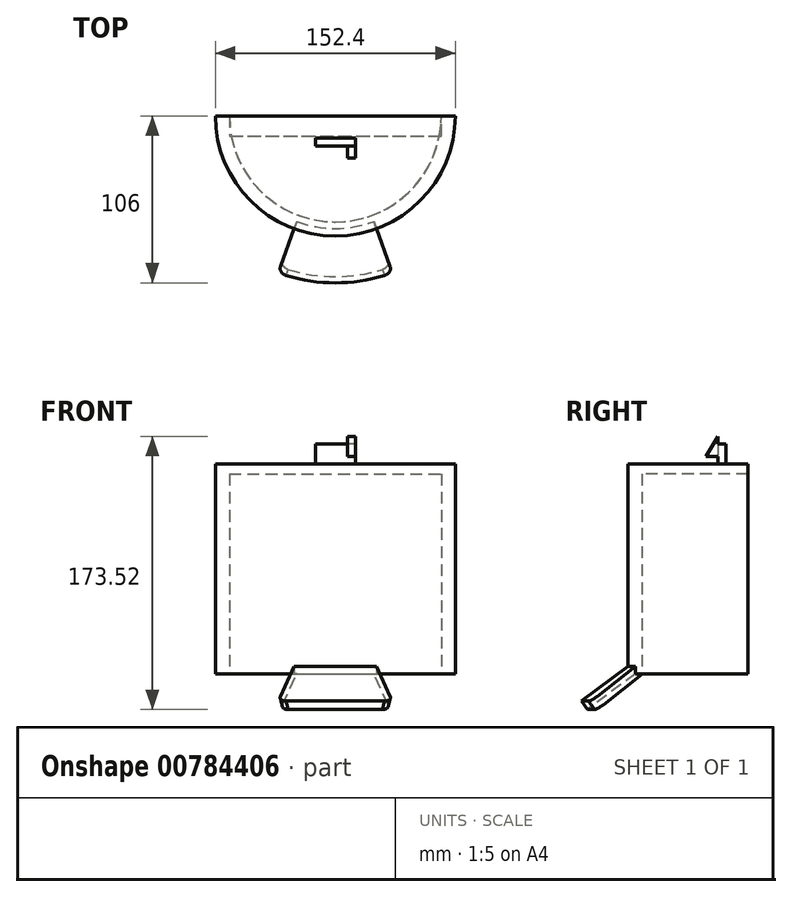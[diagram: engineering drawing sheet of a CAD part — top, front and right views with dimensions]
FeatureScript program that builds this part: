
annotation { "Feature Type Name" : "Feature", "Feature Type Description" : "" }
export const myFeature = defineFeature(function(context is Context, id is Id, definition is map)
    precondition{}
    {
        {
            var Q0;
            Q0=qCreatedBy(makeId("Top.planeOp"),FACE);
            var sketch = newSketch(context, id + "F0", { "sketchPlane" : qUnion([Q0])});
            skArc(sketch, "E0", {"start": v(76.2, 0) * mm, "mid": v(0, -76.2) * mm, "end": v(-76.2, 0) * mm});
            skLineSegment(sketch, "E1", {"start": v(-67.31, 0) * mm, "end": v(-67.31, -12.7) * mm});
            skLineSegment(sketch, "E2", {"start": v(-67.31, -12.7) * mm, "end": v(67.31, -12.7) * mm});
            skLineSegment(sketch, "E3", {"start": v(67.31, -12.7) * mm, "end": v(67.31, 0) * mm});
            skLineSegment(sketch, "E4", {"start": v(67.31, 0) * mm, "end": v(76.2, 0) * mm});
            skLineSegment(sketch, "E5", {"start": v(-76.2, 0) * mm, "end": v(-67.31, 0) * mm});
            skSolve(sketch);
        }
        {
            var Q0;
            Q0=qSketchRegion(id+"F0",true);
            extrude(context, id + "F1", {"entities" : qUnion([Q0]), "depth" : 3 / 406.4 * mm, "offsetDistance" : 25.4 * mm});
        }
        {
            var Q0;
            Q0=makeQuery(id+"F1.opExtrude","CAP_FACE",FACE,{"disambiguationData":[OSD([sQuery(id+"F0.wireOp",EDGE,"E0"),sQuery(id+"F0.wireOp",EDGE,"E1"),sQuery(id+"F0.wireOp",EDGE,"E2"),sQuery(id+"F0.wireOp",EDGE,"E3"),sQuery(id+"F0.wireOp",EDGE,"E4"),sQuery(id+"F0.wireOp",EDGE,"E5")])],"isStart":false});
            var sketch = newSketch(context, id + "F2", { "sketchPlane" : qUnion([Q0])});
            skArc(sketch, "E6", {"start": v(-76.2, 0) * mm, "mid": v(0, -76.2) * mm, "end": v(76.2, 0) * mm});
            skArc(sketch, "E7", {"start": v(-67.31, 0) * mm, "mid": v(0, -67.31) * mm, "end": v(67.31, 0) * mm});
            skLineSegment(sketch, "E8", {"start": v(-67.31, 0) * mm, "end": v(-76.2, 0) * mm});
            skLineSegment(sketch, "E9", {"start": v(67.31, 0) * mm, "end": v(76.2, 0) * mm});
            skSolve(sketch);
        }
        {
            var Q0;
            Q0=qSketchRegion(id+"F2",true);
            extrude(context, id + "F3", {"entities" : qUnion([Q0]), "operationType" : NewBodyOperationType.ADD, "depth" : 127 * mm, "offsetDistance" : 25.4 * mm});
        }
        {
            var Q0;
            Q0=makeQuery(id+"F3.opExtrude","CAP_FACE",FACE,{"disambiguationData":[OSD([sQuery(id+"F2.wireOp",EDGE,"E6"),sQuery(id+"F2.wireOp",EDGE,"E7"),sQuery(id+"F2.wireOp",EDGE,"E8"),sQuery(id+"F2.wireOp",EDGE,"E9")])],"isStart":false});
            var sketch = newSketch(context, id + "F4", { "sketchPlane" : qUnion([Q0])});
            skArc(sketch, "E10", {"start": v(-76.2, 0) * mm, "mid": v(0, -76.2) * mm, "end": v(76.2, 0) * mm});
            skLineSegment(sketch, "E11", {"start": v(-76.2, 0) * mm, "end": v(76.2, 0) * mm});
            skSolve(sketch);
        }
        {
            var Q0;
            Q0=qSketchRegion(id+"F4",true);
            extrude(context, id + "F5", {"entities" : qUnion([Q0]), "operationType" : NewBodyOperationType.ADD, "depth" : 6.35 * mm, "offsetDistance" : 25.4 * mm});
        }
        {
            var Q0;
            Q0=makeQuery(id+"F5.opExtrude","CAP_FACE",FACE,{"disambiguationData":[OSD([sQuery(id+"F4.wireOp",EDGE,"E10"),sQuery(id+"F4.wireOp",EDGE,"E11")])],"isStart":false});
            var sketch = newSketch(context, id + "F6", { "sketchPlane" : qUnion([Q0])});
            skLineSegment(sketch, "E12", {"start": v(-33.63, 0) * mm, "end": v(36.5, 0) * mm, "construction": true});
            skLineSegment(sketch, "E13", {"start": v(0, 0) * mm, "end": v(0, -25.4) * mm, "construction": true});
            skLineSegment(sketch, "E14", {"start": v(0, -14.09) * mm, "end": v(-12.7, -14.09) * mm});
            skLineSegment(sketch, "E15", {"start": v(-12.7, -14.09) * mm, "end": v(-12.7, -19.17) * mm});
            skLineSegment(sketch, "E16", {"start": v(0, -19.17) * mm, "end": v(-12.7, -19.17) * mm});
            skLineSegment(sketch, "E17.MirrorCS", {"start": v(0, -19.17) * mm, "end": v(12.7, -19.17) * mm});
            skLineSegment(sketch, "E18.MirrorCS", {"start": v(0, -14.09) * mm, "end": v(12.7, -14.09) * mm});
            skLineSegment(sketch, "E19.MirrorCS", {"start": v(12.7, -14.09) * mm, "end": v(12.7, -19.17) * mm});
            skSolve(sketch);
        }
        {
            var Q0;
            Q0=qSketchRegion(id+"F6",true);
            extrude(context, id + "F7", {"entities" : qUnion([Q0]), "operationType" : NewBodyOperationType.ADD, "depth" : 12.7 * mm, "offsetDistance" : 25.4 * mm});
        }
        {
            var Q0;
            Q0=makeQuery(id+"F7.opExtrude","SWEPT_FACE",FACE,{"disambiguationData":[OSD([sQuery(id+"F6.wireOp",EDGE,"E19.MirrorCS")])]});
            var sketch = newSketch(context, id + "F8", { "sketchPlane" : qUnion([Q0])});
            skLineSegment(sketch, "E20", {"start": v(-14.09, 138.11) * mm, "end": v(-26.79, 138.11) * mm, "construction": true});
            skLineSegment(sketch, "E21", {"start": v(-26.79, 138.11) * mm, "end": v(-19.17, 150.81) * mm});
            skLineSegment(sketch, "E22", {"start": v(-19.17, 150.81) * mm, "end": v(-19.17, 138.11) * mm});
            skLineSegment(sketch, "E23", {"start": v(-19.17, 138.11) * mm, "end": v(-26.79, 138.11) * mm});
            skSolve(sketch);
        }
        {
            var Q0;
            Q0=qSketchRegion(id+"F8",true);
            extrude(context, id + "F9", {"entities" : qUnion([Q0]), "operationType" : NewBodyOperationType.ADD, "oppositeDirection" : true, "depth" : 5.08 * mm, "offsetDistance" : 25.4 * mm});
        }
        {
            var Q0;
            Q0=qCreatedBy(makeId("Right.planeOp"),FACE);
            var sketch = newSketch(context, id + "F10", { "sketchPlane" : qUnion([Q0])});
            skLineSegment(sketch, "E24", {"start": v(0, 0) * mm, "end": v(-76.2, 0) * mm, "construction": true});
            skLineSegment(sketch, "E25", {"start": v(-69.5, 0) * mm, "end": v(-98.69, -24.5) * mm});
            skLineSegment(sketch, "E26", {"start": v(-76.2, 5.16) * mm, "end": v(-104.3, -17.81) * mm});
            skLineSegment(sketch, "E27", {"start": v(-104.3, -17.81) * mm, "end": v(-98.69, -24.5) * mm});
            skLineSegment(sketch, "E28", {"start": v(-76.2, 5.16) * mm, "end": v(-76.2, 0) * mm});
            skLineSegment(sketch, "E29", {"start": v(-76.2, 0) * mm, "end": v(-69.5, 0) * mm});
            skSolve(sketch);
        }
        {
            var Q0;
            Q0=makeQuery(id+"F10.imprint","IMPRINT",FACE,{"disambiguationData":[TD([[makeQuery(id+"F10.imprint","IMPRINT",EDGE,{"derivedFrom":sQuery(id+"F10.wireOp",EDGE,"E25")}),-1.0]])]});
            var Q1;
            Q1=makeQuery(id+"F5.boolean.opBoolean","MERGE",FACE,{"derivedFrom":[makeQuery(id+"F3.boolean.opBoolean","MERGE",FACE,{"derivedFrom":[makeQuery(id+"F1.opExtrude","SWEPT_FACE",FACE,{"disambiguationData":[OSD([sQuery(id+"F0.wireOp",EDGE,"E0")])]}),makeQuery(id+"F3.opExtrude","SWEPT_FACE",FACE,{"disambiguationData":[OSD([sQuery(id+"F2.wireOp",EDGE,"E6")])]})]}),makeQuery(id+"F5.opExtrude","SWEPT_FACE",FACE,{"disambiguationData":[OSD([sQuery(id+"F4.wireOp",EDGE,"E10")])]})]});
            revolve(context, id + "F11", {"surfaceOperationType" : NewSurfaceOperationType.NEW, "entities" : qUnion([Q0]), "axis" : qUnion([Q1]), "revolveType" : RevolveType.TWO_DIRECTIONS, "angle" : 20 * degree, "angleBack" : 340 * degree});
        }
        {
            var Q0;
            Q0=makeQuery(id+"F11.opRevolve","CAP_EDGE",EDGE,{"disambiguationData":[OSD([sQuery(id+"F10.wireOp",EDGE,"E27")])],"isStart":true});
            var Q1;
            Q1=makeQuery(id+"F11.opRevolve","CAP_EDGE",EDGE,{"disambiguationData":[OSD([sQuery(id+"F10.wireOp",EDGE,"E27")])],"isStart":false});
            fillet(context, id + "F12", {"entities" : qUnion([Q0, Q1]), "radius" : 5.08 * mm, "tangentPropagation" : true, "allowEdgeOverflow" : false});
        }
        {
            var Q0;
            Q0=makeQuery(id+"F11.opRevolve","SWEPT_BODY",BODY,{"disambiguationData":[OSD([sQuery(id+"F10.wireOp",EDGE,"E25"),sQuery(id+"F10.wireOp",EDGE,"E26"),sQuery(id+"F10.wireOp",EDGE,"E27"),sQuery(id+"F10.wireOp",EDGE,"E28"),sQuery(id+"F10.wireOp",EDGE,"E29")])]});
            deleteBodies(context, id + "F13", {"entities" : qUnion([Q0])});
        }
        {
            var Q0;
            Q0=qCreatedBy(makeId("Right.planeOp"),FACE);
            var sketch = newSketch(context, id + "F14", { "sketchPlane" : qUnion([Q0])});
            skLineSegment(sketch, "E30", {"start": v(0, 0) * mm, "end": v(-76.2, 0) * mm, "construction": true});
            skLineSegment(sketch, "E31", {"start": v(-76.2, 0) * mm, "end": v(-76.2, 54.42) * mm, "construction": true});
            skLineSegment(sketch, "E32", {"start": v(-76.2, 4.76) * mm, "end": v(-106, -17.36) * mm});
            skLineSegment(sketch, "E33", {"start": v(-106, -17.36) * mm, "end": v(-102.03, -22.71) * mm});
            skLineSegment(sketch, "E34", {"start": v(-102.03, -22.71) * mm, "end": v(-71.44, 0) * mm});
            skLineSegment(sketch, "E35", {"start": v(-76.2, 4.76) * mm, "end": v(-76.2, 0) * mm});
            skLineSegment(sketch, "E36", {"start": v(-71.44, 0) * mm, "end": v(-76.2, 0) * mm});
            skSolve(sketch);
        }
        {
            var Q0;
            Q0 = qSketchRegion(id + "F14", true);
            var Q1;
            Q1=makeQuery(id+"F5.boolean.opBoolean","MERGE",FACE,{"derivedFrom":[makeQuery(id+"F3.boolean.opBoolean","MERGE",FACE,{"derivedFrom":[makeQuery(id+"F1.opExtrude","SWEPT_FACE",FACE,{"disambiguationData":[OSD([sQuery(id+"F0.wireOp",EDGE,"E0")])]}),makeQuery(id+"F3.opExtrude","SWEPT_FACE",FACE,{"disambiguationData":[OSD([sQuery(id+"F2.wireOp",EDGE,"E6")])]})]}),makeQuery(id+"F5.opExtrude","SWEPT_FACE",FACE,{"disambiguationData":[OSD([sQuery(id+"F4.wireOp",EDGE,"E10")])]})]});
            revolve(context, id + "F15", {"operationType" : NewBodyOperationType.ADD, "surfaceOperationType" : NewSurfaceOperationType.NEW, "entities" : qUnion([Q0]), "axis" : qUnion([Q1]), "revolveType" : RevolveType.TWO_DIRECTIONS, "angle" : 20 * degree, "angleBack" : 340 * degree});
        }
        {
            var Q0;
            Q0=makeQuery(id+"F15.opRevolve","CAP_EDGE",EDGE,{"disambiguationData":[OSD([sQuery(id+"F14.wireOp",EDGE,"E33")])],"isStart":true});
            var Q1;
            Q1=makeQuery(id+"F15.opRevolve","CAP_EDGE",EDGE,{"disambiguationData":[OSD([sQuery(id+"F14.wireOp",EDGE,"E33")])],"isStart":false});
            fillet(context, id + "F16", {"entities" : qUnion([Q0, Q1]), "radius" : 5.08 * mm, "tangentPropagation" : true, "allowEdgeOverflow" : false});
        }
    });
